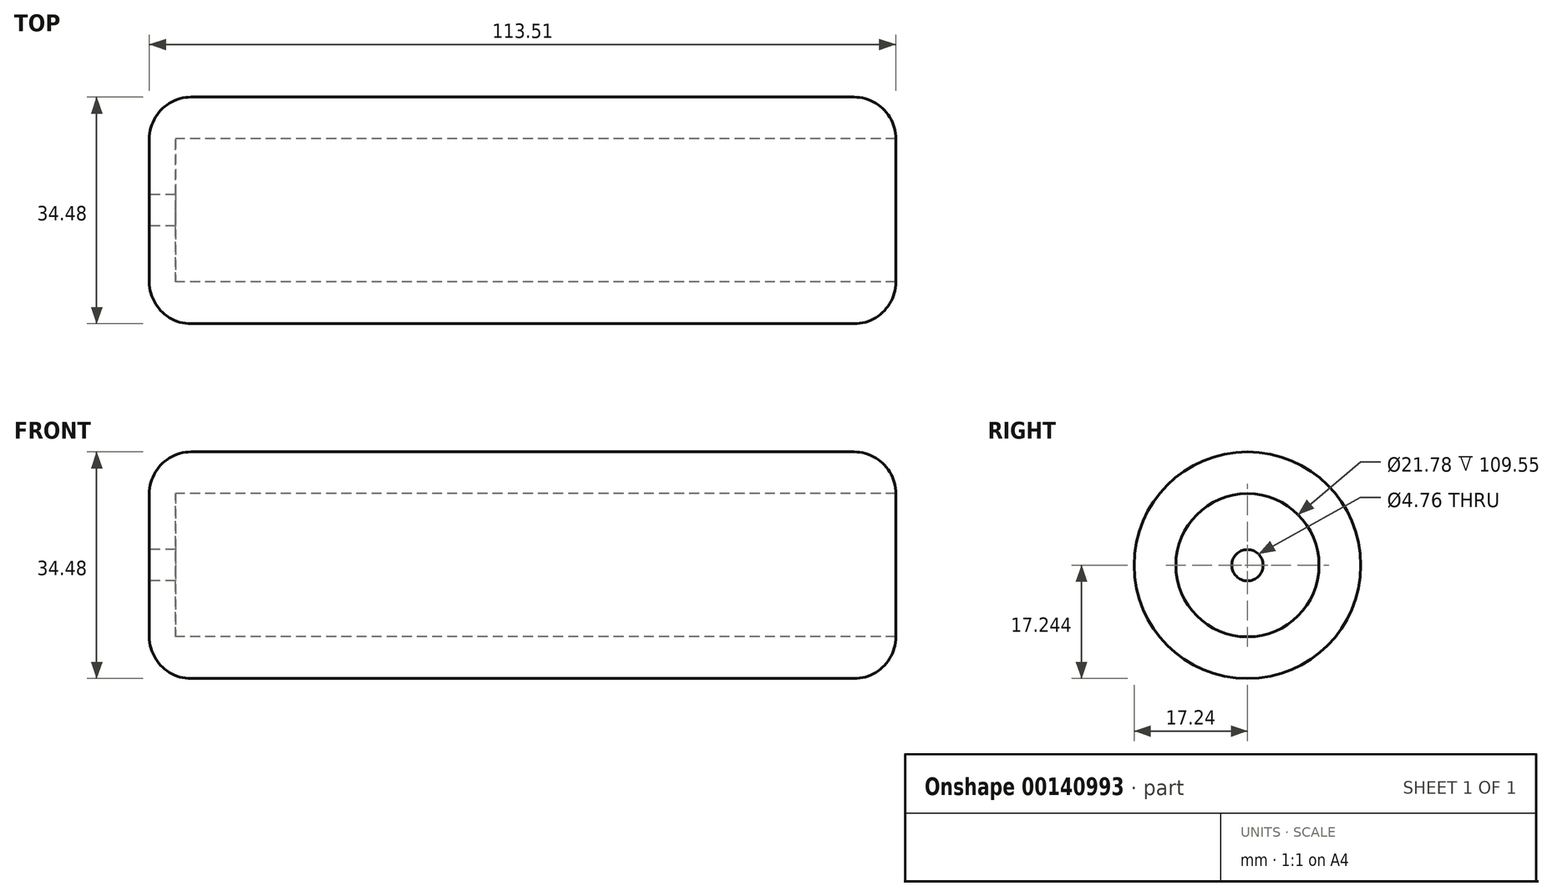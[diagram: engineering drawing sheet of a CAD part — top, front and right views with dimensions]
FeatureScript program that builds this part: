
annotation { "Feature Type Name" : "Feature", "Feature Type Description" : "" }
export const myFeature = defineFeature(function(context is Context, id is Id, definition is map)
    precondition{}
    {
        {
            var Q0;
            Q0=qCreatedBy(makeId("Front.planeOp"),FACE);
            var sketch = newSketch(context, id + "F0", { "sketchPlane" : qUnion([Q0])});
            skLineSegment(sketch, "E0", {"start": v(6.35, -8.97) * mm, "end": v(107.16, -8.97) * mm});
            skLineSegment(sketch, "E1", {"start": v(113.51, -2.62) * mm, "end": v(113.51, -2.62) * mm});
            skLineSegment(sketch, "E2", {"start": v(113.51, -2.62) * mm, "end": v(3.96, -2.62) * mm});
            skPoint(sketch, "E3.orphan", {"position": v(3.96, -7.1) * mm});
            skPoint(sketch, "E4.visualSharp", {"position": v(0, -8.97) * mm});
            skArc(sketch, "E4.filletArc", {"start": v(0, -2.62) * mm, "mid": v(1.86, -7.1) * mm, "end": v(6.35, -8.97) * mm});
            skPoint(sketch, "E5.visualSharp", {"position": v(113.51, -8.97) * mm});
            skArc(sketch, "E5.filletArc", {"start": v(107.16, -8.97) * mm, "mid": v(111.65, -7.1) * mm, "end": v(113.51, -2.62) * mm});
            skLineSegment(sketch, "E6", {"start": v(0, -2.62) * mm, "end": v(0, 5.9) * mm});
            skLineSegment(sketch, "E7", {"start": v(0, 5.9) * mm, "end": v(3.96, 5.9) * mm});
            skLineSegment(sketch, "E8", {"start": v(3.96, -2.62) * mm, "end": v(3.96, 5.9) * mm});
            skLineSegment(sketch, "E9", {"start": v(0, 5.9) * mm, "end": v(0, 8.27) * mm, "construction": true});
            skLineSegment(sketch, "E10", {"start": v(0, 8.27) * mm, "end": v(25, 8.27) * mm, "construction": true});
            skSolve(sketch);
        }
        {
            var Q0;
            Q0=makeQuery(id+"F0.imprint","IMPRINT",FACE,{"disambiguationData":[TD([[makeQuery(id+"F0.imprint","IMPRINT",EDGE,{"derivedFrom":sQuery(id+"F0.wireOp",EDGE,"E0")}),1.0]])]});
            var Q1;
            Q1=sQuery(id+"F0.wireOp",EDGE,"E10");
            revolve(context, id + "F1", {"entities" : qUnion([Q0]), "axis" : qUnion([Q1]), "revolveType" : RevolveType.FULL});
        }
    });
